# Revit family: Footlight
name_source: partatom
category: Lighting Fixtures
revit_build: Autodesk Revit LT 2015 (Build: 20140606_1530(x64)
units: mm (PartAtom-declared; Revit-internal decimal feet)

## types (2) — shared parameters
BIMObjectName = Footlight
BallastCELMAEnergyEfficiencyIndex = See driver specification
Beam Width = Extra Wide
CableLength = 200 mm  [stored 0.656168 ft]
CableSize = 2 off 7/0.2 Tinned Copper Strands
CableType = 2 Core PVC
Color Filter = 16777215
CurrentRating = 350mA
Default Elevation = 1200 mm
Description = Mini surface mounted display light
Dimming Lamp Color Temperature Shift = <None>
DurationUnit = year
Efficacy = 63 lm/W
ExpectedLife = Lifetime L70/B10 >50,000 hrs
ForwardVoltage = 2.8V DC
IngressProtection = IP10
InsulationStandardClass = Class III
Keynote = Technical data figures are for guidance only and are subject to ±5% tolerance
LampColourRendering = ≥90 Ra
LampColourTemperature = 2700K
LampLumens = 92 lm
LampType = LED
LuminaireLumens = 63 lm
Manufacturer = John Cullen Lighting Ltd
ManufacturerName = John Cullen Lighting Ltd
ManufacturerURL = www.johncullenlighting.co.uk
Material = Aluminium
MaxAmbientTemperature = 50.00°
Model = Footlight
NBSDescription = General purpose luminaires are described by characteristics such as standards, photometric performance and supply circuit conductor connections.
An example use may be within a hard wired general lighting system.
Name = Footlight
NominalHeight = 55 mm  [stored 0.180446 ft]
NominalLength = 28 mm  [stored 0.0918635 ft]
NominalWidth = 28 mm  [stored 0.0918635 ft]
ProductInformation = http://www.johncullenlighting.co.uk
Shape = Cylindrical
Size = 28(D)x55(H)
Tilt Angle = 0.00°
URL = http://www.johncullenlighting.co.uk
Uniclass2 = Pr_70_70_48_85 Surface luminaires
Version = 1
WarrantyDescription = Refer to John Cullen Lighting Ltd - Terms and Conditions document
WarrantyDurationLabor = www.johncullenlighting.co.uk/terms_and_conditions/
WarrantyDurationParts = www.johncullenlighting.co.uk/terms_and_conditions/
WarrantyDurationUnit = www.johncullenlighting.co.uk/terms_and_conditions/
WarrantyGuarantorLabor = www.johncullenlighting.co.uk/terms_and_conditions/
WarrantyGuarantorParts = www.johncullenlighting.co.uk/terms_and_conditions/
Wattage = 1 W
Weight = 60

## per-type parameters (varying)
| type | CodePerformance | Color | Finish | ModelNumber | Photometric Web File |
| Footlight/1W/350mA/927/Bronze | SCMF27061 | Bronze | Bronze | SCMF27061 | FootlightBronze-350.IES |
| Footlight/1W/350mA/927/Aluminium | SCMF27101 | Aluminium | Aluminium | SCMF27101 | FootlightAluminium-350.IES |

note: [stored X ft] marks values corroborated as IEEE doubles in the binary element streams (Revit-internal decimal feet)

## geometry (parser evidence)
native form markers: Sweep x3
no freeform markers — native parametric forms only
